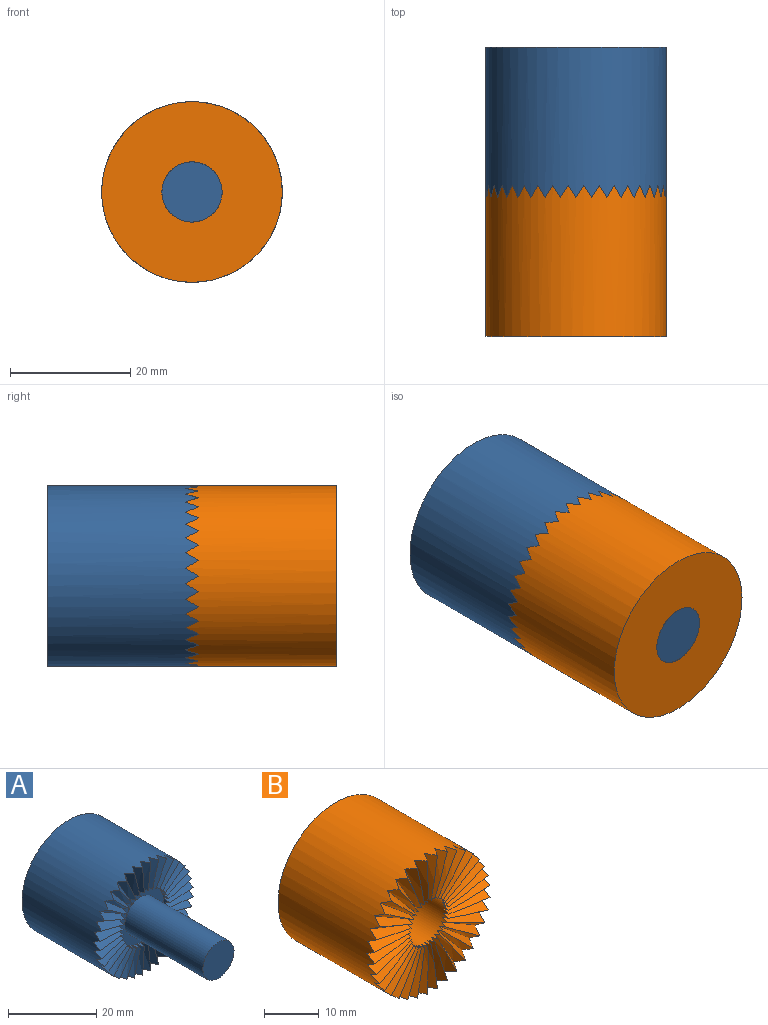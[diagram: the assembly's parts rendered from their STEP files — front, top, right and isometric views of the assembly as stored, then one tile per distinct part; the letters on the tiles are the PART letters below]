
ASSEMBLY  parts=2 mates=1
PART A: 113 faces, bbox 31x48x31 mm
  f0: cylinder r=7.5mm len=1.88mm, axis (0,-1,0), area 1.2mm2, adj f38,f40,f109
  f1: cylinder r=7.5mm len=1.88mm, axis (0,-1,0), area 1.2mm2, adj f38,f107,f110
  f2: cylinder r=7.5mm len=1.88mm, axis (0,-1,0), area 1.2mm2, adj f38,f105,f108
  f3: cylinder r=7.5mm len=1.88mm, axis (0,-1,0), area 1.2mm2, adj f38,f103,f106
  f4: cylinder r=7.5mm len=1.88mm, axis (0,-1,0), area 1.2mm2, adj f38,f101,f104
  f5: cylinder r=7.5mm len=1.88mm, axis (0,-1,0), area 1.2mm2, adj f38,f99,f102
  f6: cylinder r=7.5mm len=1.88mm, axis (0,-1,0), area 1.2mm2, adj f38,f97,f100
  f7: cylinder r=7.5mm len=1.88mm, axis (0,-1,0), area 1.2mm2, adj f38,f95,f98
  f8: cylinder r=7.5mm len=1.88mm, axis (0,-1,0), area 1.2mm2, adj f38,f93,f96
  f9: cylinder r=7.5mm len=1.88mm, axis (0,-1,0), area 1.2mm2, adj f38,f91,f94
  f10: cylinder r=7.5mm len=1.88mm, axis (0,-1,0), area 1.2mm2, adj f38,f89,f92
  f11: cylinder r=7.5mm len=1.88mm, axis (0,-1,0), area 1.2mm2, adj f38,f87,f90
  f12: cylinder r=7.5mm len=1.88mm, axis (0,-1,0), area 1.2mm2, adj f38,f85,f88
  f13: cylinder r=7.5mm len=1.88mm, axis (0,-1,0), area 1.2mm2, adj f38,f83,f86
  f14: cylinder r=7.5mm len=1.88mm, axis (0,-1,0), area 1.2mm2, adj f38,f81,f84
  f15: cylinder r=7.5mm len=1.88mm, axis (0,-1,0), area 1.2mm2, adj f38,f79,f82
  f16: cylinder r=7.5mm len=1.88mm, axis (0,-1,0), area 1.2mm2, adj f38,f77,f80
  f17: cylinder r=7.5mm len=1.88mm, axis (0,-1,0), area 1.2mm2, adj f38,f75,f78
  f18: cylinder r=7.5mm len=1.88mm, axis (0,-1,0), area 1.2mm2, adj f38,f73,f76
  f19: cylinder r=7.5mm len=1.88mm, axis (0,-1,0), area 1.2mm2, adj f38,f71,f74
  f20: cylinder r=7.5mm len=1.88mm, axis (0,-1,0), area 1.2mm2, adj f38,f69,f72
  f21: cylinder r=7.5mm len=1.88mm, axis (0,-1,0), area 1.2mm2, adj f38,f67,f70
  f22: cylinder r=7.5mm len=1.88mm, axis (0,-1,0), area 1.2mm2, adj f38,f65,f68
  f23: cylinder r=7.5mm len=1.88mm, axis (0,-1,0), area 1.2mm2, adj f38,f63,f66
  f24: cylinder r=7.5mm len=1.88mm, axis (0,-1,0), area 1.2mm2, adj f38,f61,f64
  f25: cylinder r=7.5mm len=1.88mm, axis (0,-1,0), area 1.2mm2, adj f38,f59,f62
  f26: cylinder r=7.5mm len=1.88mm, axis (0,-1,0), area 1.2mm2, adj f38,f57,f60
  f27: cylinder r=7.5mm len=1.88mm, axis (0,-1,0), area 1.2mm2, adj f38,f55,f58
  f28: cylinder r=7.5mm len=1.88mm, axis (0,-1,0), area 1.2mm2, adj f38,f53,f56
  f29: cylinder r=7.5mm len=1.88mm, axis (0,-1,0), area 1.2mm2, adj f38,f51,f54
  f30: cylinder r=7.5mm len=1.88mm, axis (0,-1,0), area 1.2mm2, adj f38,f49,f52
  f31: cylinder r=7.5mm len=1.88mm, axis (0,-1,0), area 1.2mm2, adj f38,f47,f50
  f32: cylinder r=7.5mm len=1.88mm, axis (0,-1,0), area 1.2mm2, adj f38,f45,f48
  f33: cylinder r=7.5mm len=1.88mm, axis (0,-1,0), area 1.2mm2, adj f38,f43,f46
  f34: cylinder r=7.5mm len=1.88mm, axis (0,-1,0), area 1.2mm2, adj f38,f41,f44
  f35: cylinder r=15mm len=30mm, axis (0,-1,0), area 2261.7mm2, adj f36,f39,f40,f41,f42,f43,f44,f45
  f36: plane 30x30mm, normal (0,1,0), area 706.9mm2, adj f35
  f37: cylinder r=7.5mm len=1.88mm, axis (0,-1,0), area 1.2mm2, adj f38,f39,f42
  f38: plane 15x15mm, normal (0,-1,0), area 98.2mm2, adj f0,f1,f2,f3,f4,f5,f6,f7
  f39: bspline ~8.5x2mm, area 16.3mm2, adj f35,f37,f40,f42
  f40: bspline ~8.5x2mm, area 16.3mm2, adj f0,f35,f39,f109
  f41: bspline ~8.49x2.81mm, area 16.3mm2, adj f34,f35,f42,f44
  f42: bspline ~8.61x2.12mm, area 16.3mm2, adj f35,f37,f39,f41
  f43: bspline ~8.21x4.18mm, area 16.3mm2, adj f33,f35,f44,f46
  f44: bspline ~8.45x3.52mm, area 16.3mm2, adj f34,f35,f41,f43
  f45: bspline ~7.69x5.42mm, area 16.3mm2, adj f32,f35,f46,f48
  f46: bspline ~8.04x4.82mm, area 16.3mm2, adj f33,f35,f43,f45
  f47: bspline ~6.93x6.5mm, area 16.3mm2, adj f31,f35,f48,f50
  f48: bspline ~7.38x5.97mm, area 16.3mm2, adj f32,f35,f45,f47
  f49: bspline ~7.38x5.97mm, area 16.3mm2, adj f30,f35,f50,f52
  f50: bspline ~6.93x6.5mm, area 16.3mm2, adj f31,f35,f47,f49
  f51: bspline ~8.04x4.82mm, area 16.3mm2, adj f29,f35,f52,f54
  f52: bspline ~7.69x5.42mm, area 16.3mm2, adj f30,f35,f49,f51
  f53: bspline ~8.45x3.52mm, area 16.3mm2, adj f28,f35,f54,f56
  f54: bspline ~8.21x4.18mm, area 16.3mm2, adj f29,f35,f51,f53
  f55: bspline ~8.61x2.12mm, area 16.3mm2, adj f27,f35,f56,f58
  f56: bspline ~8.49x2.81mm, area 16.3mm2, adj f28,f35,f53,f55
  f57: bspline ~8.5x2mm, area 16.3mm2, adj f26,f35,f58,f60
  f58: bspline ~8.5x2mm, area 16.3mm2, adj f27,f35,f55,f57
  f59: bspline ~8.49x2.81mm, area 16.3mm2, adj f25,f35,f60,f62
  f60: bspline ~8.61x2.12mm, area 16.3mm2, adj f26,f35,f57,f59
  f61: bspline ~8.21x4.18mm, area 16.3mm2, adj f24,f35,f62,f64
  f62: bspline ~8.45x3.52mm, area 16.3mm2, adj f25,f35,f59,f61
  f63: bspline ~7.69x5.42mm, area 16.3mm2, adj f23,f35,f64,f66
  f64: bspline ~8.04x4.82mm, area 16.3mm2, adj f24,f35,f61,f63
  f65: bspline ~6.93x6.5mm, area 16.3mm2, adj f22,f35,f66,f68
  f66: bspline ~7.38x5.97mm, area 16.3mm2, adj f23,f35,f63,f65
  f67: bspline ~7.38x5.97mm, area 16.3mm2, adj f21,f35,f68,f70
  f68: bspline ~6.93x6.5mm, area 16.3mm2, adj f22,f35,f65,f67
  f69: bspline ~8.04x4.82mm, area 16.3mm2, adj f20,f35,f70,f72
  f70: bspline ~7.69x5.42mm, area 16.3mm2, adj f21,f35,f67,f69
  f71: bspline ~8.45x3.52mm, area 16.3mm2, adj f19,f35,f72,f74
  f72: bspline ~8.21x4.18mm, area 16.3mm2, adj f20,f35,f69,f71
  f73: bspline ~8.61x2.12mm, area 16.3mm2, adj f18,f35,f74,f76
  f74: bspline ~8.49x2.81mm, area 16.3mm2, adj f19,f35,f71,f73
  f75: bspline ~8.5x2mm, area 16.3mm2, adj f17,f35,f76,f78
  f76: bspline ~8.5x2mm, area 16.3mm2, adj f18,f35,f73,f75
  f77: bspline ~8.49x2.81mm, area 16.3mm2, adj f16,f35,f78,f80
  f78: bspline ~8.61x2.12mm, area 16.3mm2, adj f17,f35,f75,f77
  f79: bspline ~8.21x4.18mm, area 16.3mm2, adj f15,f35,f80,f82
  f80: bspline ~8.45x3.52mm, area 16.3mm2, adj f16,f35,f77,f79
  f81: bspline ~7.69x5.42mm, area 16.3mm2, adj f14,f35,f82,f84
  f82: bspline ~8.04x4.82mm, area 16.3mm2, adj f15,f35,f79,f81
  f83: bspline ~6.93x6.5mm, area 16.3mm2, adj f13,f35,f84,f86
  f84: bspline ~7.38x5.97mm, area 16.3mm2, adj f14,f35,f81,f83
  f85: bspline ~7.38x5.97mm, area 16.3mm2, adj f12,f35,f86,f88
  f86: bspline ~6.93x6.5mm, area 16.3mm2, adj f13,f35,f83,f85
  f87: bspline ~8.04x4.82mm, area 16.3mm2, adj f11,f35,f88,f90
  f88: bspline ~7.69x5.42mm, area 16.3mm2, adj f12,f35,f85,f87
  f89: bspline ~8.45x3.52mm, area 16.3mm2, adj f10,f35,f90,f92
  f90: bspline ~8.21x4.18mm, area 16.3mm2, adj f11,f35,f87,f89
  f91: bspline ~8.61x2.12mm, area 16.3mm2, adj f9,f35,f92,f94
  f92: bspline ~8.49x2.81mm, area 16.3mm2, adj f10,f35,f89,f91
  f93: bspline ~8.5x2mm, area 16.3mm2, adj f8,f35,f94,f96
  f94: bspline ~8.5x2mm, area 16.3mm2, adj f9,f35,f91,f93
  f95: bspline ~8.49x2.81mm, area 16.3mm2, adj f7,f35,f96,f98
  f96: bspline ~8.61x2.12mm, area 16.3mm2, adj f8,f35,f93,f95
  f97: bspline ~8.21x4.18mm, area 16.3mm2, adj f6,f35,f98,f100
  f98: bspline ~8.45x3.52mm, area 16.3mm2, adj f7,f35,f95,f97
  f99: bspline ~7.69x5.42mm, area 16.3mm2, adj f5,f35,f100,f102
  f100: bspline ~8.04x4.82mm, area 16.3mm2, adj f6,f35,f97,f99
  f101: bspline ~6.93x6.5mm, area 16.3mm2, adj f4,f35,f102,f104
  f102: bspline ~7.38x5.97mm, area 16.3mm2, adj f5,f35,f99,f101
  f103: bspline ~7.38x5.97mm, area 16.3mm2, adj f3,f35,f104,f106
  f104: bspline ~6.93x6.5mm, area 16.3mm2, adj f4,f35,f101,f103
  f105: bspline ~8.04x4.82mm, area 16.3mm2, adj f2,f35,f106,f108
  f106: bspline ~7.69x5.42mm, area 16.3mm2, adj f3,f35,f103,f105
  f107: bspline ~8.45x3.52mm, area 16.3mm2, adj f1,f35,f108,f110
  f108: bspline ~8.21x4.18mm, area 16.3mm2, adj f2,f35,f105,f107
  f109: bspline ~8.61x2.12mm, area 16.3mm2, adj f0,f35,f40,f110
  f110: bspline ~8.49x2.81mm, area 16.3mm2, adj f1,f35,f107,f109
  f111: cylinder r=5mm len=25mm, axis (0,1,0), area 785.4mm2, adj f38,f112
  f112: plane 10x10mm, normal (0,-1,0), area 78.5mm2, adj f111
PART B: 75 faces, bbox 30.1x25x30.1 mm
  f0: cylinder r=15mm len=30mm, axis (0,-1,0), area 2261.7mm2, adj f1,f2,f3,f4,f5,f6,f7,f8
  f1: plane 30x30mm, normal (0,1,0), area 628.2mm2, adj f0,f74
  f2: bspline ~10.24x2mm, area 18.5mm2, adj f0,f3,f4,f74
  f3: bspline ~10.24x2mm, area 18.5mm2, adj f0,f2,f72,f74
  f4: bspline ~10.31x2.42mm, area 18.5mm2, adj f0,f2,f5,f74
  f5: bspline ~10.2x3.07mm, area 18.5mm2, adj f0,f4,f6,f74
  f6: bspline ~10.07x4.12mm, area 18.5mm2, adj f0,f5,f7,f74
  f7: bspline ~9.85x4.74mm, area 18.5mm2, adj f0,f6,f8,f74
  f8: bspline ~9.53x5.69mm, area 18.5mm2, adj f0,f7,f9,f74
  f9: bspline ~9.2x6.26mm, area 18.5mm2, adj f0,f8,f10,f74
  f10: bspline ~8.69x7.08mm, area 18.5mm2, adj f0,f9,f11,f74
  f11: bspline ~8.27x7.59mm, area 18.5mm2, adj f0,f10,f12,f74
  f12: bspline ~8.27x7.59mm, area 18.5mm2, adj f0,f11,f13,f74
  f13: bspline ~8.69x7.08mm, area 18.5mm2, adj f0,f12,f14,f74
  f14: bspline ~9.2x6.26mm, area 18.5mm2, adj f0,f13,f15,f74
  f15: bspline ~9.53x5.69mm, area 18.5mm2, adj f0,f14,f16,f74
  f16: bspline ~9.85x4.74mm, area 18.5mm2, adj f0,f15,f17,f74
  f17: bspline ~10.07x4.12mm, area 18.5mm2, adj f0,f16,f18,f74
  f18: bspline ~10.2x3.07mm, area 18.5mm2, adj f0,f17,f19,f74
  f19: bspline ~10.31x2.42mm, area 18.5mm2, adj f0,f18,f20,f74
  f20: bspline ~10.24x2mm, area 18.5mm2, adj f0,f19,f21,f74
  f21: bspline ~10.24x2mm, area 18.5mm2, adj f0,f20,f22,f74
  f22: bspline ~10.31x2.42mm, area 18.5mm2, adj f0,f21,f23,f74
  f23: bspline ~10.2x3.07mm, area 18.5mm2, adj f0,f22,f24,f74
  f24: bspline ~10.07x4.12mm, area 18.5mm2, adj f0,f23,f25,f74
  f25: bspline ~9.85x4.74mm, area 18.5mm2, adj f0,f24,f26,f74
  f26: bspline ~9.53x5.69mm, area 18.5mm2, adj f0,f25,f27,f74
  f27: bspline ~9.2x6.26mm, area 18.5mm2, adj f0,f26,f28,f74
  f28: bspline ~8.69x7.08mm, area 18.5mm2, adj f0,f27,f29,f74
  f29: bspline ~8.27x7.59mm, area 18.5mm2, adj f0,f28,f30,f74
  f30: bspline ~8.27x7.59mm, area 18.5mm2, adj f0,f29,f31,f74
  f31: bspline ~8.69x7.08mm, area 18.5mm2, adj f0,f30,f32,f74
  f32: bspline ~9.2x6.26mm, area 18.5mm2, adj f0,f31,f33,f74
  f33: bspline ~9.53x5.69mm, area 18.5mm2, adj f0,f32,f34,f74
  f34: bspline ~9.85x4.74mm, area 18.5mm2, adj f0,f33,f35,f74
  f35: bspline ~10.07x4.12mm, area 18.5mm2, adj f0,f34,f36,f74
  f36: bspline ~10.2x3.07mm, area 18.5mm2, adj f0,f35,f37,f74
  f37: bspline ~10.31x2.42mm, area 18.5mm2, adj f0,f36,f38,f74
  f38: bspline ~10.24x2mm, area 18.5mm2, adj f0,f37,f39,f74
  f39: bspline ~10.24x2mm, area 18.5mm2, adj f0,f38,f40,f74
  f40: bspline ~10.31x2.42mm, area 18.5mm2, adj f0,f39,f41,f74
  f41: bspline ~10.2x3.07mm, area 18.5mm2, adj f0,f40,f42,f74
  f42: bspline ~10.07x4.12mm, area 18.5mm2, adj f0,f41,f43,f74
  f43: bspline ~9.85x4.74mm, area 18.5mm2, adj f0,f42,f44,f74
  f44: bspline ~9.53x5.69mm, area 18.5mm2, adj f0,f43,f45,f74
  f45: bspline ~9.2x6.26mm, area 18.5mm2, adj f0,f44,f46,f74
  f46: bspline ~8.69x7.08mm, area 18.5mm2, adj f0,f45,f47,f74
  f47: bspline ~8.27x7.59mm, area 18.5mm2, adj f0,f46,f48,f74
  f48: bspline ~8.27x7.59mm, area 18.5mm2, adj f0,f47,f49,f74
  f49: bspline ~8.69x7.08mm, area 18.5mm2, adj f0,f48,f50,f74
  f50: bspline ~9.2x6.26mm, area 18.5mm2, adj f0,f49,f51,f74
  f51: bspline ~9.53x5.69mm, area 18.5mm2, adj f0,f50,f52,f74
  f52: bspline ~9.85x4.74mm, area 18.5mm2, adj f0,f51,f53,f74
  f53: bspline ~10.07x4.12mm, area 18.5mm2, adj f0,f52,f54,f74
  f54: bspline ~10.2x3.07mm, area 18.5mm2, adj f0,f53,f55,f74
  f55: bspline ~10.31x2.42mm, area 18.5mm2, adj f0,f54,f56,f74
  f56: bspline ~10.24x2mm, area 18.5mm2, adj f0,f55,f57,f74
  f57: bspline ~10.24x2mm, area 18.5mm2, adj f0,f56,f58,f74
  f58: bspline ~10.31x2.42mm, area 18.5mm2, adj f0,f57,f59,f74
  f59: bspline ~10.2x3.07mm, area 18.5mm2, adj f0,f58,f60,f74
  f60: bspline ~10.07x4.12mm, area 18.5mm2, adj f0,f59,f61,f74
  f61: bspline ~9.85x4.74mm, area 18.5mm2, adj f0,f60,f62,f74
  f62: bspline ~9.53x5.69mm, area 18.5mm2, adj f0,f61,f63,f74
  f63: bspline ~9.2x6.26mm, area 18.5mm2, adj f0,f62,f64,f74
  f64: bspline ~8.69x7.08mm, area 18.5mm2, adj f0,f63,f65,f74
  f65: bspline ~8.27x7.59mm, area 18.5mm2, adj f0,f64,f66,f74
  f66: bspline ~8.27x7.59mm, area 18.5mm2, adj f0,f65,f67,f74
  f67: bspline ~8.69x7.08mm, area 18.5mm2, adj f0,f66,f68,f74
  f68: bspline ~9.2x6.26mm, area 18.5mm2, adj f0,f67,f69,f74
  f69: bspline ~9.53x5.69mm, area 18.5mm2, adj f0,f68,f70,f74
  f70: bspline ~9.85x4.74mm, area 18.5mm2, adj f0,f69,f71,f74
  f71: bspline ~10.07x4.12mm, area 18.5mm2, adj f0,f70,f73,f74
  f72: bspline ~10.31x2.42mm, area 18.5mm2, adj f0,f3,f73,f74
  f73: bspline ~10.2x3.07mm, area 18.5mm2, adj f0,f71,f72,f74
  f74: cylinder r=5mm len=24.31mm, axis (0,-1,0), area 743.4mm2, adj f1,f2,f3,f4,f5,f6,f7,f8
PLACE A rot(axis=(0,-1,0),15deg) t=(-1.95,-35.95,9.25)mm
PLACE B rot(axis=(0.17,0,-0.98),180deg) t=(-1.95,-33.95,9.25)mm
MATE fastened B.f74 <-> A.f111  axis (0,1,0) through (-1.95,-33.95,9.25)mm
